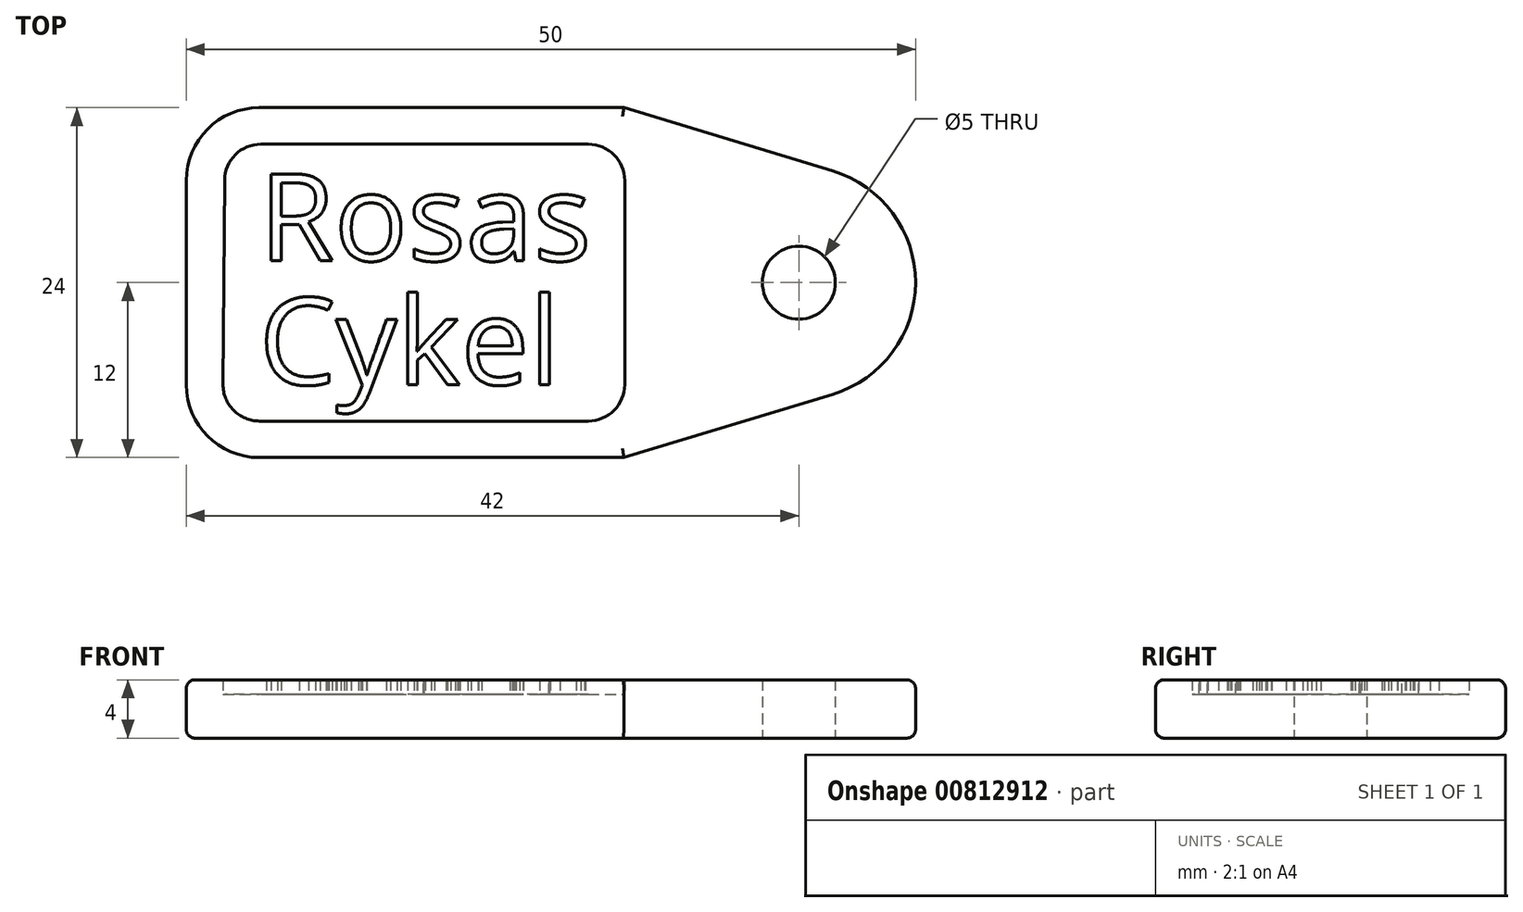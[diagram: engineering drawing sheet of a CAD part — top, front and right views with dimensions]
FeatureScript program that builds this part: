
annotation { "Feature Type Name" : "Feature", "Feature Type Description" : "" }
export const myFeature = defineFeature(function(context is Context, id is Id, definition is map)
    precondition{}
    {
        {
            var Q0;
            Q0=qCreatedBy(makeId("Top.planeOp"),FACE);
            var sketch = newSketch(context, id + "F0", { "sketchPlane" : qUnion([Q0])});
            skLineSegment(sketch, "E0", {"start": v(5, 12) * mm, "end": v(30, 12) * mm});
            skLineSegment(sketch, "E1", {"start": v(30, 12) * mm, "end": v(44.32, 7.66) * mm});
            skLineSegment(sketch, "E2", {"start": v(44.32, -7.66) * mm, "end": v(30, -12) * mm});
            skLineSegment(sketch, "E3", {"start": v(30, -12) * mm, "end": v(5, -12) * mm});
            skLineSegment(sketch, "E4", {"start": v(0, -7) * mm, "end": v(0, 7) * mm});
            skPoint(sketch, "E5.visualSharp", {"position": v(69.56, 0) * mm});
            skArc(sketch, "E5.filletArc", {"start": v(44.32, -7.66) * mm, "mid": v(50, 0) * mm, "end": v(44.32, 7.66) * mm});
            skPoint(sketch, "E6.visualSharp", {"position": v(0, 12) * mm});
            skArc(sketch, "E6.filletArc", {"start": v(5, 12) * mm, "mid": v(1.46, 10.54) * mm, "end": v(0, 7) * mm});
            skPoint(sketch, "E7.visualSharp", {"position": v(0, -12) * mm});
            skArc(sketch, "E7.filletArc", {"start": v(0, -7) * mm, "mid": v(1.46, -10.54) * mm, "end": v(5, -12) * mm});
            skSolve(sketch);
        }
        {
            var Q0;
            Q0=makeQuery(id+"F0.imprint","IMPRINT",FACE,{"disambiguationData":[TD([[makeQuery(id+"F0.imprint","IMPRINT",EDGE,{"derivedFrom":sQuery(id+"F0.wireOp",EDGE,"E0")}),-1.0]])]});
            extrude(context, id + "F1", {"entities" : qUnion([Q0]), "depth" : 3 * mm, "offsetDistance" : 25 * mm});
        }
        {
            var Q0;
            Q0=makeQuery(id+"F1.opExtrude","CAP_FACE",FACE,{"disambiguationData":[OSD([sQuery(id+"F0.wireOp",EDGE,"E0"),sQuery(id+"F0.wireOp",EDGE,"E1"),sQuery(id+"F0.wireOp",EDGE,"E2"),sQuery(id+"F0.wireOp",EDGE,"E3"),sQuery(id+"F0.wireOp",EDGE,"E4"),sQuery(id+"F0.wireOp",EDGE,"E5.filletArc"),sQuery(id+"F0.wireOp",EDGE,"E6.filletArc"),sQuery(id+"F0.wireOp",EDGE,"E7.filletArc")])],"isStart":false});
            var sketch = newSketch(context, id + "F2", { "sketchPlane" : qUnion([Q0])});
            skPoint(sketch, "E8.visualSharp", {"position": v(30, 12) * mm});
            skText(sketch, "E9", { "text": "Rosas", "fontName": "OpenSans-Regular.ttf"});
            skPoint(sketch, "E10", {"position": v(5, -7) * mm});
            skText(sketch, "E11", { "text": "Cykel", "fontName": "OpenSans-Regular.ttf"});
            skLineSegment(sketch, "E12", {"start": v(5.13, 9.5) * mm, "end": v(27.56, 9.5) * mm});
            skLineSegment(sketch, "E13", {"start": v(30.06, 7) * mm, "end": v(30.06, -7) * mm});
            skLineSegment(sketch, "E14", {"start": v(27.56, -9.5) * mm, "end": v(5.02, -9.5) * mm});
            skLineSegment(sketch, "E15", {"start": v(2.52, -6.98) * mm, "end": v(2.63, 7.02) * mm});
            skPoint(sketch, "E16.visualSharp", {"position": v(2.65, 9.5) * mm});
            skArc(sketch, "E16.filletArc", {"start": v(5.13, 9.5) * mm, "mid": v(3.37, 8.77) * mm, "end": v(2.63, 7.02) * mm});
            skPoint(sketch, "E17.visualSharp", {"position": v(2.5, -9.5) * mm});
            skArc(sketch, "E17.filletArc", {"start": v(2.52, -6.98) * mm, "mid": v(3.24, -8.76) * mm, "end": v(5.02, -9.5) * mm});
            skPoint(sketch, "E18.visualSharp", {"position": v(30.06, -9.5) * mm});
            skArc(sketch, "E18.filletArc", {"start": v(27.56, -9.5) * mm, "mid": v(29.33, -8.77) * mm, "end": v(30.06, -7) * mm});
            skPoint(sketch, "E19.visualSharp", {"position": v(30.06, 9.5) * mm});
            skArc(sketch, "E19.filletArc", {"start": v(30.06, 7) * mm, "mid": v(29.33, 8.77) * mm, "end": v(27.56, 9.5) * mm});
            const initialGuessF2  = {"E9": [0.005, 0.0015, 1, 0, 0.006], "E11": [0.005, -0.007, 1, 0, 0.006]};
            skSetInitialGuess(sketch, initialGuessF2);
            skSolve(sketch);
        }
        {
            var Q0;
            Q0=makeQuery(id+"F2.imprint","IMPRINT",FACE,{"disambiguationData":[TD([[makeQuery(id+"F2.imprint","IMPRINT",EDGE,{"derivedFrom":sQuery(id+"F2.wireOp",EDGE,"E9.sketch_text.stroke-18")}),-1.0]])]});
            var Q1;
            Q1=makeQuery(id+"F2.imprint","IMPRINT",FACE,{"disambiguationData":[TD([[makeQuery(id+"F2.imprint","IMPRINT",EDGE,{"derivedFrom":sQuery(id+"F2.wireOp",EDGE,"E9.sketch_text.stroke-0")}),-1.0]])]});
            var Q2;
            Q2=makeQuery(id+"F2.imprint","IMPRINT",FACE,{"disambiguationData":[TD([[makeQuery(id+"F2.imprint","IMPRINT",EDGE,{"derivedFrom":sQuery(id+"F2.wireOp",EDGE,"E9.sketch_text.stroke-35")}),-1.0]])]});
            var Q3;
            Q3=makeQuery(id+"F2.imprint","IMPRINT",FACE,{"disambiguationData":[TD([[makeQuery(id+"F2.imprint","IMPRINT",EDGE,{"derivedFrom":sQuery(id+"F2.wireOp",EDGE,"E9.sketch_text.stroke-60")}),-1.0]])]});
            var Q4;
            Q4=makeQuery(id+"F2.imprint","IMPRINT",FACE,{"disambiguationData":[TD([[makeQuery(id+"F2.imprint","IMPRINT",EDGE,{"derivedFrom":sQuery(id+"F2.wireOp",EDGE,"E9.sketch_text.stroke-87")}),-1.0]])]});
            var Q5;
            Q5=makeQuery(id+"F2.imprint","IMPRINT",FACE,{"disambiguationData":[TD([[makeQuery(id+"F2.imprint","IMPRINT",EDGE,{"derivedFrom":sQuery(id+"F2.wireOp",EDGE,"E11.sketch_text.stroke-0")}),-1.0]])]});
            var Q6;
            Q6=makeQuery(id+"F2.imprint","IMPRINT",FACE,{"disambiguationData":[TD([[makeQuery(id+"F2.imprint","IMPRINT",EDGE,{"derivedFrom":sQuery(id+"F2.wireOp",EDGE,"E11.sketch_text.stroke-15")}),-1.0]])]});
            var Q7;
            Q7=makeQuery(id+"F2.imprint","IMPRINT",FACE,{"disambiguationData":[TD([[makeQuery(id+"F2.imprint","IMPRINT",EDGE,{"derivedFrom":sQuery(id+"F2.wireOp",EDGE,"E11.sketch_text.stroke-31")}),-1.0]])]});
            var Q8;
            Q8=makeQuery(id+"F2.imprint","IMPRINT",FACE,{"disambiguationData":[TD([[makeQuery(id+"F2.imprint","IMPRINT",EDGE,{"derivedFrom":sQuery(id+"F2.wireOp",EDGE,"E11.sketch_text.stroke-46")}),-1.0]])]});
            var Q9;
            Q9=makeQuery(id+"F2.imprint","IMPRINT",FACE,{"disambiguationData":[TD([[makeQuery(id+"F2.imprint","IMPRINT",EDGE,{"derivedFrom":sQuery(id+"F2.wireOp",EDGE,"E11.sketch_text.stroke-65")}),-1.0]])]});
            extrude(context, id + "F3", {"entities" : qUnion([Q0, Q1, Q2, Q3, Q4, Q5, Q6, Q7, Q8, Q9]), "operationType" : NewBodyOperationType.ADD, "depth" : 1 * mm, "offsetDistance" : 25 * mm});
        }
        {
            var Q0;
            Q0=makeQuery(id+"F1.opExtrude","CAP_EDGE",EDGE,{"disambiguationData":[OSD([sQuery(id+"F0.wireOp",EDGE,"E7.filletArc")])],"isStart":true});
            var Q1;
            Q1=makeQuery(id+"F1.opExtrude","CAP_EDGE",EDGE,{"disambiguationData":[OSD([sQuery(id+"F0.wireOp",EDGE,"E2")])],"isStart":true});
            fillet(context, id + "F4", {"entities" : qUnion([Q0, Q1]), "radius" : .6 * mm, "tangentPropagation" : true, "allowEdgeOverflow" : false});
        }
        {
            var Q0;
            Q0=makeQuery(id+"F2.imprint","IMPRINT",FACE,{"disambiguationData":[TD([[makeQuery(id+"F2.imprint","IMPRINT",EDGE,{"derivedFrom":sQuery(id+"F2.wireOp",EDGE,"E12")}),1.0]])]});
            extrude(context, id + "F5", {"entities" : qUnion([Q0]), "operationType" : NewBodyOperationType.ADD, "depth" : 1 * mm, "offsetDistance" : 25 * mm});
        }
        {
            var Q0;
            Q0=sQuery(id+"F0.wireOp",VERTEX,"E5.filletArc.center");
            var Q1;
            Q1=makeQuery(id+"F1.opExtrude","SWEPT_BODY",BODY,{"disambiguationData":[OSD([sQuery(id+"F0.wireOp",EDGE,"E0"),sQuery(id+"F0.wireOp",EDGE,"E1"),sQuery(id+"F0.wireOp",EDGE,"E2"),sQuery(id+"F0.wireOp",EDGE,"E3"),sQuery(id+"F0.wireOp",EDGE,"E4"),sQuery(id+"F0.wireOp",EDGE,"E5.filletArc"),sQuery(id+"F0.wireOp",EDGE,"E6.filletArc"),sQuery(id+"F0.wireOp",EDGE,"E7.filletArc")])]});
            hole(context, id + "F6", {"style" : HoleStyle.SIMPLE, "endStyle" : HoleEndStyle.THROUGH, "oppositeDirection" : true, "holeDiameter" : 5 * mm, "majorDiameter" : 5 * mm, "isTappedThrough" : true, "tappedDepth" : 12 * mm, "tapClearance" : 3, "locations" : qUnion([Q0]), "scope" : qUnion([Q1])});
        }
        {
            var Q0;
            Q0=makeQuery(id+"F5.opExtrude","CAP_EDGE",EDGE,{"disambiguationData":[OSD([sQuery(id+"F0.wireOp",EDGE,"E0")])],"isStart":false});
            var Q1;
            Q1=makeQuery(id+"F5.opExtrude","CAP_EDGE",EDGE,{"disambiguationData":[OSD([sQuery(id+"F0.wireOp",EDGE,"E1")])],"isStart":false});
            fillet(context, id + "F7", {"entities" : qUnion([Q0, Q1]), "radius" : .6 * mm, "tangentPropagation" : true, "allowEdgeOverflow" : false});
        }
    });
